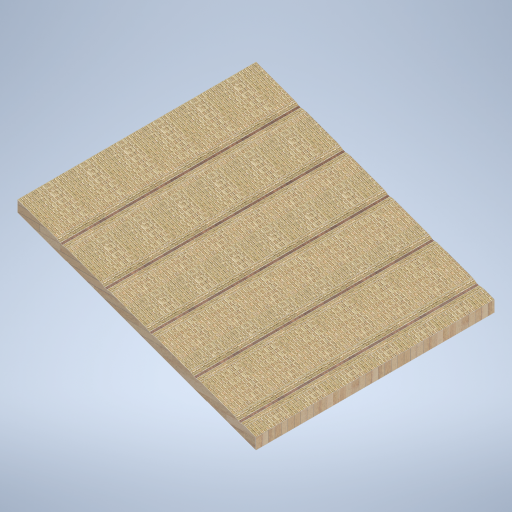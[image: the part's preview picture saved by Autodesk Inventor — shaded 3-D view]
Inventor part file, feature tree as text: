
AUTODESK INVENTOR PART (.ipt)
format: ipt  version: 2024.2 (Build 282272000, 272)  size: 546,816 bytes
history: native  units: mm
features: sketch x4, plane x3, extrude x2, fillet x1
ambient origin geometry x8: Origin, YZ Plane, XZ Plane, XY Plane, X Axis, Y Axis, Z Axis, Center Point
bodies: Solid1 (feature_tree)
feature tree (10):
  sketch  "Sketch1"  dims[d0=100.0mm d1=2111.0mm]
  plane  "Work Plane2"
  sketch  "Sketch3"  dims[d2=0.0mm d3=2109.0mm d4=19.198622mm d5=19.198622mm]
  plane  "Work Plane3"
  extrude  "Extrusion1"  Depth=2111.0mm
  extrude  "Extrusion2"  Depth=2109.0mm
  fillet  "Fillet1"  Radius=19.198622mm
  plane  "Work Plane1"
  sketch  "Sketch4"  dims[d6=2111.0mm d7=0.0mm]
  sketch  "Sketch5"  dims[d8=400.0mm d9=10.0mm d10=20.0mm d11=400.0mm d12=20.0mm d13=400.0mm d14=20.0mm d15=400.0mm d16=20.0mm d17=400.0mm d18=20.0mm d19=0.0mm d20=0.0mm d21=100.0mm]
